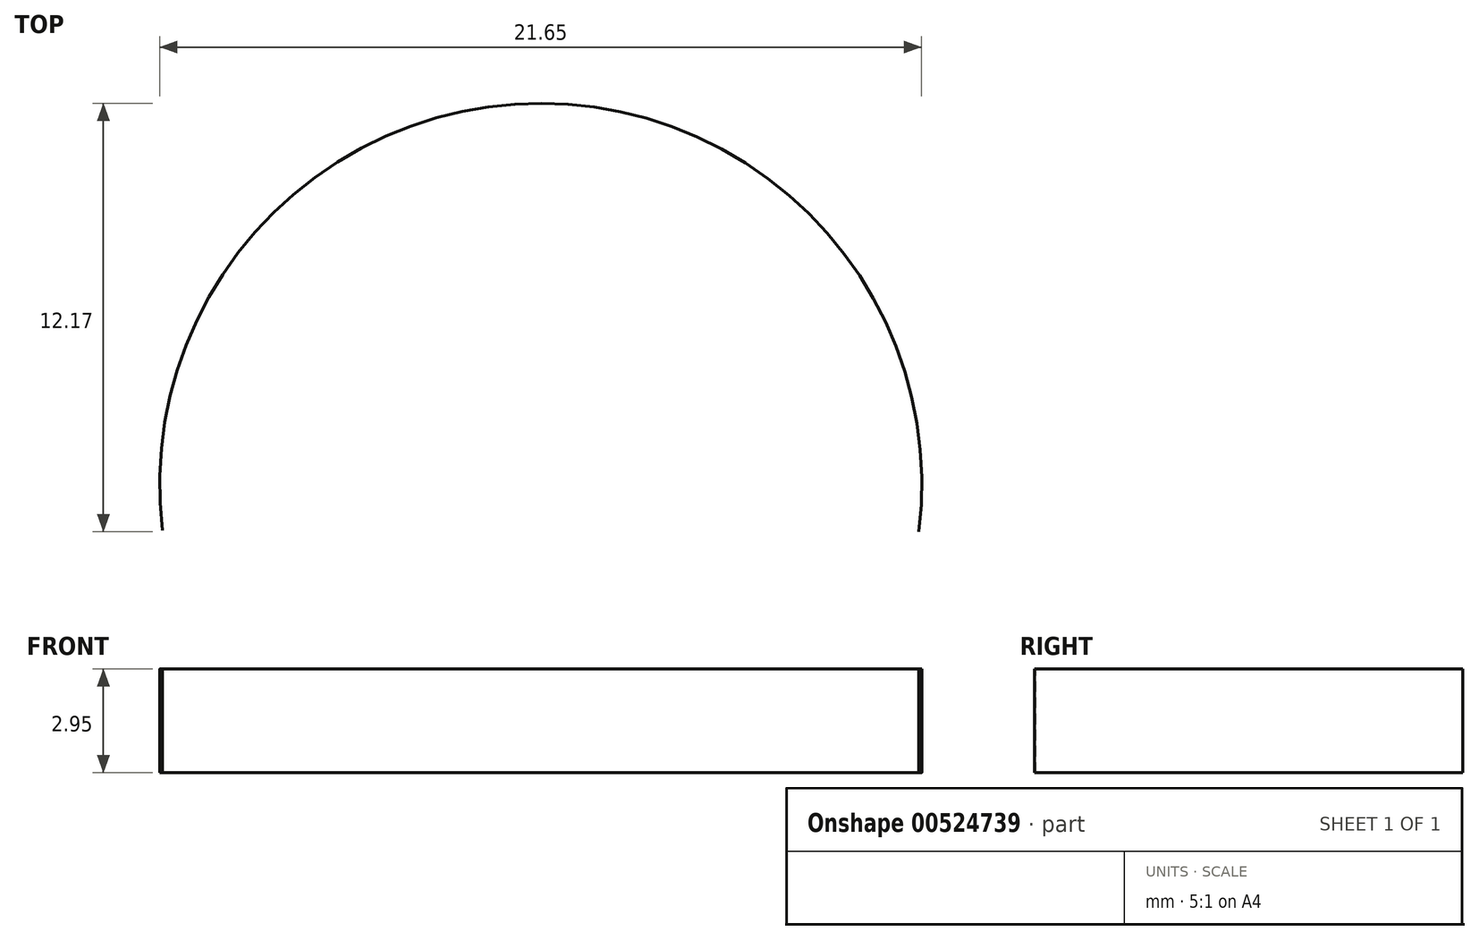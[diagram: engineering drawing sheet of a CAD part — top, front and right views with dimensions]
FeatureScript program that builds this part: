
annotation { "Feature Type Name" : "Feature", "Feature Type Description" : "" }
export const myFeature = defineFeature(function(context is Context, id is Id, definition is map)
    precondition{}
    {
        {
            var Q0;
            Q0=qCreatedBy(makeId("Top.planeOp"),FACE);
            var sketch = newSketch(context, id + "F0", { "sketchPlane" : qUnion([Q0])});
            skArc(sketch, "E0", {"start": v(10.73, -7.69) * mm, "mid": v(0, 4.48) * mm, "end": v(-10.76, -7.65) * mm});
            skSolve(sketch);
        }
        {
            var Q0;
            Q0=sQuery(id+"F0.wireOp",EDGE,"E0");
            extrude(context, id + "F1", {"bodyType" : ToolBodyType.SURFACE, "surfaceEntities" : qUnion([Q0]), "depth" : 2.95 * mm, "offsetDistance" : 25.4 * mm});
        }
    });
